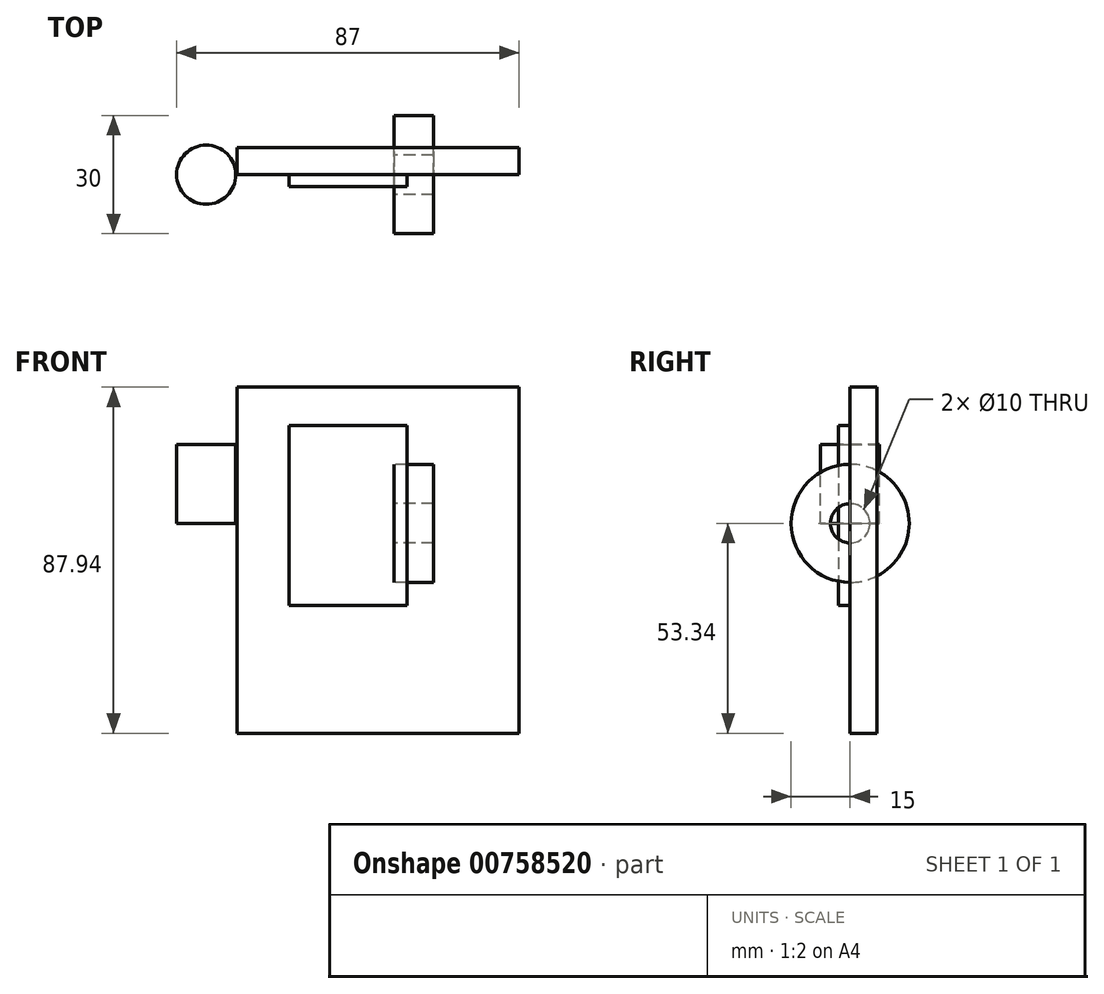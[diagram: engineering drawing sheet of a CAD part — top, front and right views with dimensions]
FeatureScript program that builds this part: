
annotation { "Feature Type Name" : "Feature", "Feature Type Description" : "" }
export const myFeature = defineFeature(function(context is Context, id is Id, definition is map)
    precondition{}
    {
        {
            var Q0;
            Q0=qCreatedBy(makeId("Front.planeOp"),FACE);
            var sketch = newSketch(context, id + "F0", { "sketchPlane" : qUnion([Q0])});
            skLineSegment(sketch, "E0", {"start": v(0, 0) * mm, "end": v(10, 0) * mm});
            skLineSegment(sketch, "E1.bottom", {"start": v(0, 15) * mm, "end": v(10, 15) * mm});
            skLineSegment(sketch, "E1.top", {"start": v(0, 5) * mm, "end": v(10, 5) * mm});
            skLineSegment(sketch, "E1.left", {"start": v(0, 15) * mm, "end": v(0, 5) * mm});
            skLineSegment(sketch, "E1.right", {"start": v(10, 15) * mm, "end": v(10, 5) * mm});
            skLineSegment(sketch, "E2.MirrorCS", {"start": v(0, -15) * mm, "end": v(10, -15) * mm});
            skLineSegment(sketch, "E3.MirrorCS", {"start": v(0, -5) * mm, "end": v(10, -5) * mm});
            skLineSegment(sketch, "E4.MirrorCS", {"start": v(0, -15) * mm, "end": v(0, -5) * mm});
            skLineSegment(sketch, "E5.MirrorCS", {"start": v(10, -15) * mm, "end": v(10, -5) * mm});
            skSolve(sketch);
        }
        {
            var Q0;
            Q0=makeQuery(id+"F0.imprint","IMPRINT",FACE,{"disambiguationData":[TD([[makeQuery(id+"F0.imprint","IMPRINT",EDGE,{"derivedFrom":sQuery(id+"F0.wireOp",EDGE,"E1.bottom")}),-1.0]])]});
            var Q1;
            Q1=makeQuery(id+"F0.imprint","IMPRINT",FACE,{"disambiguationData":[TD([[makeQuery(id+"F0.imprint","IMPRINT",EDGE,{"derivedFrom":sQuery(id+"F0.wireOp",EDGE,"E2.MirrorCS")}),1.0]])]});
            var Q2;
            Q2=sQuery(id+"F0.wireOp",EDGE,"E0");
            revolve(context, id + "F1", {"surfaceOperationType" : NewSurfaceOperationType.NEW, "entities" : qUnion([Q0, Q1]), "axis" : qUnion([Q2]), "revolveType" : RevolveType.FULL});
        }
        {
            var Q0;
            Q0=qCreatedBy(makeId("Front.planeOp"),FACE);
            var sketch = newSketch(context, id + "F2", { "sketchPlane" : qUnion([Q0])});
            skLineSegment(sketch, "E6", {"start": v(-47.78, 19.98) * mm, "end": v(-47.78, 0) * mm});
            skLineSegment(sketch, "E7.bottom", {"start": v(-55.28, 20) * mm, "end": v(-47.78, 20) * mm});
            skLineSegment(sketch, "E7.top", {"start": v(-55.28, 0) * mm, "end": v(-47.78, 0) * mm});
            skLineSegment(sketch, "E7.left", {"start": v(-55.28, 20) * mm, "end": v(-55.28, 0) * mm});
            skLineSegment(sketch, "E7.right", {"start": v(-47.78, 20) * mm, "end": v(-47.78, 0) * mm});
            skSolve(sketch);
        }
        {
            var Q0;
            {var subQ0=sQuery(id+"F2.wireOp",EDGE,"E7.bottom");Q0=makeQuery(id+"F2.imprint","IMPRINT",FACE,{"disambiguationData":[TD([[makeQuery(id+"F2.imprint","IMPRINT",EDGE,{"derivedFrom":subQ0}),-1.0]])]});}
            var Q1;
            Q1=sQuery(id+"F2.wireOp",EDGE,"E7.right");
            revolve(context, id + "F3", {"surfaceOperationType" : NewSurfaceOperationType.NEW, "entities" : qUnion([Q0]), "axis" : qUnion([Q1]), "revolveType" : RevolveType.FULL});
        }
        {
            var Q0;
            Q0=qCreatedBy(makeId("Front.planeOp"),FACE);
            var sketch = newSketch(context, id + "F4", { "sketchPlane" : qUnion([Q0])});
            skLineSegment(sketch, "E8.bottom", {"start": v(-39.95, 34.6) * mm, "end": v(31.72, 34.6) * mm});
            skLineSegment(sketch, "E8.top", {"start": v(-39.95, -53.34) * mm, "end": v(31.72, -53.34) * mm});
            skLineSegment(sketch, "E8.left", {"start": v(-39.95, 34.6) * mm, "end": v(-39.95, -53.34) * mm});
            skLineSegment(sketch, "E8.right", {"start": v(31.72, 34.6) * mm, "end": v(31.72, -53.34) * mm});
            skSolve(sketch);
        }
        {
            var Q0;
            Q0=makeQuery(id+"F4.imprint","IMPRINT",FACE,{"disambiguationData":[TD([[makeQuery(id+"F4.imprint","IMPRINT",EDGE,{"derivedFrom":sQuery(id+"F4.wireOp",EDGE,"E8.bottom")}),-1.0]])]});
            extrude(context, id + "F5", {"entities" : qUnion([Q0]), "oppositeDirection" : true, "depth" : 6.86 * mm, "offsetDistance" : 25.4 * mm});
        }
        {
            var Q0;
            Q0=qCreatedBy(makeId("Front.planeOp"),FACE);
            var sketch = newSketch(context, id + "F6", { "sketchPlane" : qUnion([Q0])});
            skLineSegment(sketch, "E9.bottom", {"start": v(-26.77, 24.92) * mm, "end": v(3.3, 24.92) * mm});
            skLineSegment(sketch, "E9.top", {"start": v(-26.77, -20.8) * mm, "end": v(3.3, -20.8) * mm});
            skLineSegment(sketch, "E9.left", {"start": v(-26.77, 24.92) * mm, "end": v(-26.77, -20.8) * mm});
            skLineSegment(sketch, "E9.right", {"start": v(3.3, 24.92) * mm, "end": v(3.3, -20.8) * mm});
            skPoint(sketch, "E10.startSnap0", {"position": v(-26.77, 2.06) * mm});
            skSolve(sketch);
        }
        {
            var Q0;
            Q0 = qSketchRegion(id + "F6", true);
            extrude(context, id + "F7", {"entities" : qUnion([Q0]), "depth" : 3 * mm, "offsetDistance" : 25.4 * mm});
        }
    });
